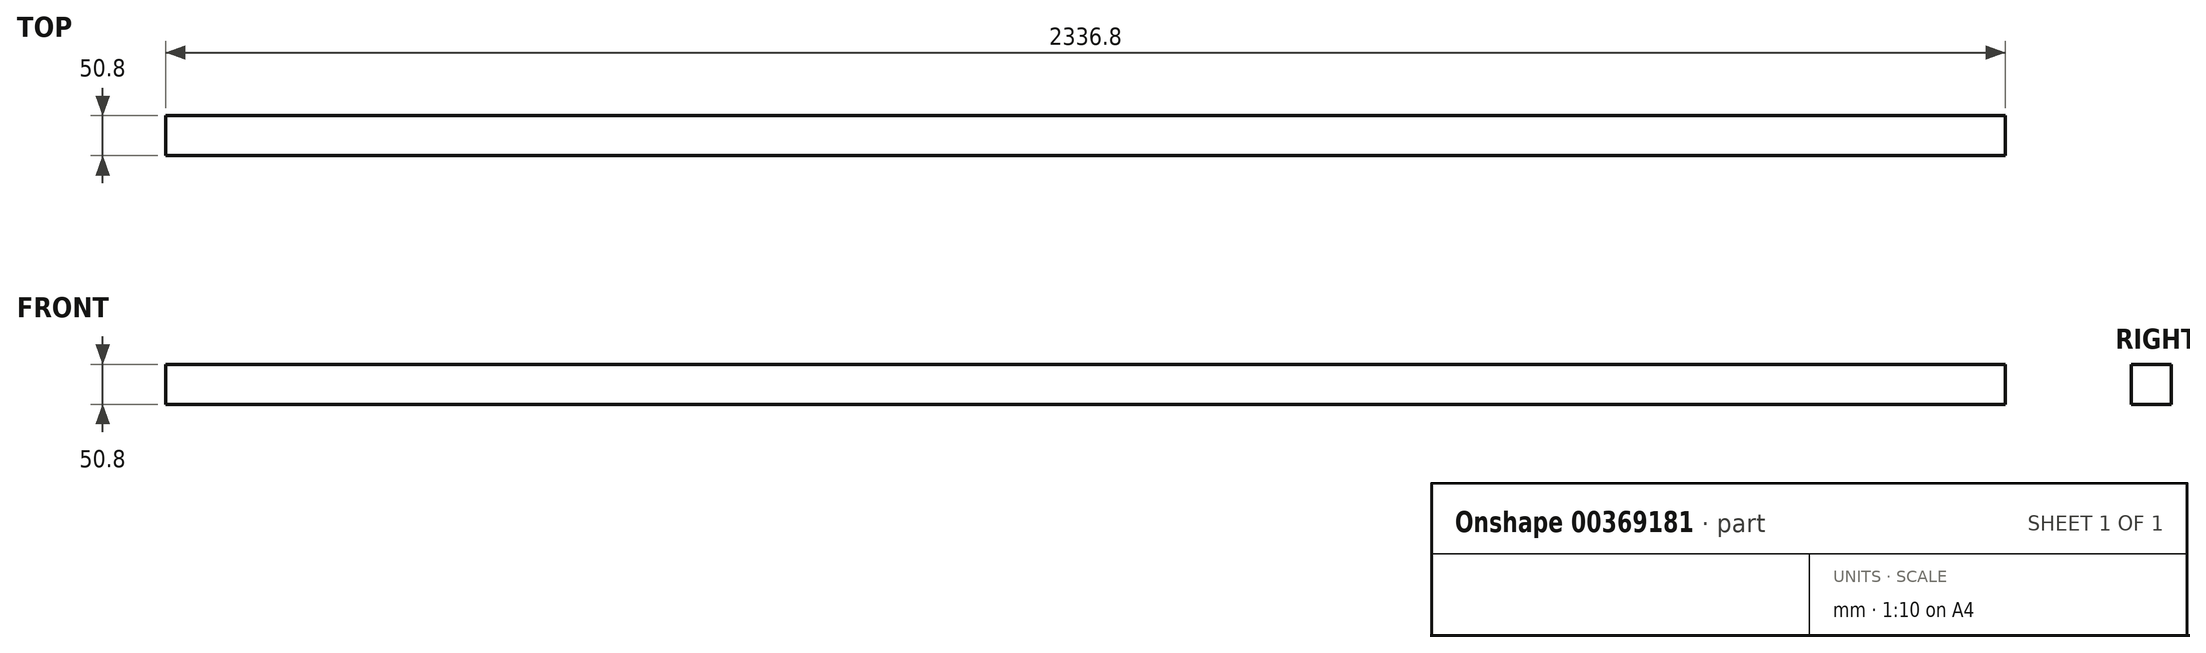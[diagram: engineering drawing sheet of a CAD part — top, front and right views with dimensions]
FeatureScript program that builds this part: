
annotation { "Feature Type Name" : "Feature", "Feature Type Description" : "" }
export const myFeature = defineFeature(function(context is Context, id is Id, definition is map)
    precondition{}
    {
        {
            var Q0;
            Q0=qCreatedBy(makeId("Front.planeOp"),FACE);
            var sketch = newSketch(context, id + "F0", { "sketchPlane" : qUnion([Q0])});
            skLineSegment(sketch, "E0", {"start": v(-1201.9, -13.12) * mm, "end": v(-1201.9, -63.92) * mm});
            skLineSegment(sketch, "E1", {"start": v(-1201.9, -63.92) * mm, "end": v(1134.9, -63.92) * mm});
            skLineSegment(sketch, "E2", {"start": v(-1201.9, -13.12) * mm, "end": v(1134.9, -13.12) * mm});
            skLineSegment(sketch, "E3", {"start": v(1134.9, -13.12) * mm, "end": v(1134.9, -63.92) * mm});
            skSolve(sketch);
        }
        {
            var Q0;
            Q0=makeQuery(id+"F0.imprint","IMPRINT",FACE,{"disambiguationData":[TD([[makeQuery(id+"F0.imprint","IMPRINT",EDGE,{"derivedFrom":sQuery(id+"F0.wireOp",EDGE,"E0")}),1.0]])]});
            extrude(context, id + "F1", {"entities" : qUnion([Q0]), "depth" : 50.8 * mm});
        }
    });
